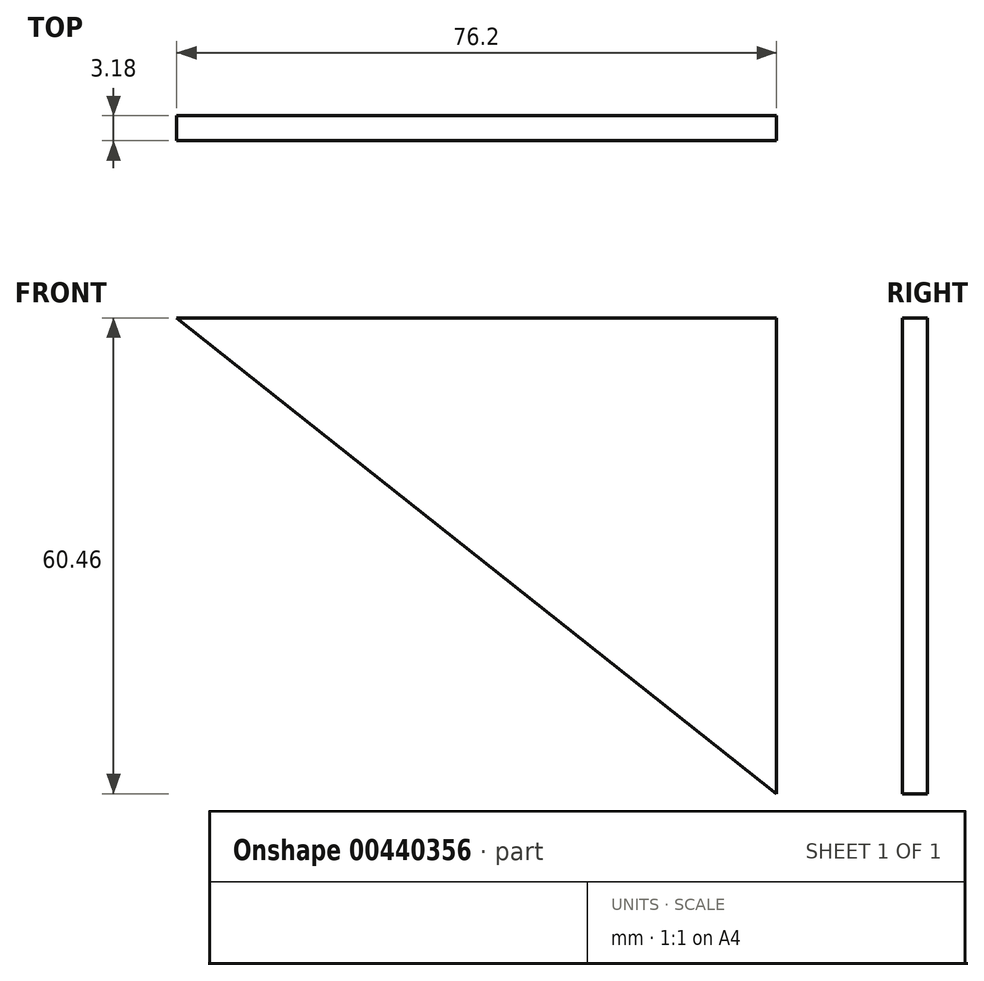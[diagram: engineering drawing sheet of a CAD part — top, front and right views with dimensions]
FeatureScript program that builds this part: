
annotation { "Feature Type Name" : "Feature", "Feature Type Description" : "" }
export const myFeature = defineFeature(function(context is Context, id is Id, definition is map)
    precondition{}
    {
        {
            var Q0;
            Q0=qCreatedBy(makeId("Front.planeOp"),FACE);
            var sketch = newSketch(context, id + "F0", { "sketchPlane" : qUnion([Q0])});
            skLineSegment(sketch, "E0.bottom", {"start": v(-38.1, 30.23) * mm, "end": v(38.1, 30.23) * mm});
            skLineSegment(sketch, "E0.right", {"start": v(38.1, 30.23) * mm, "end": v(38.1, -30.23) * mm});
            skPoint(sketch, "E0.middle", {"position": v(0, 0) * mm});
            skLineSegment(sketch, "E1", {"start": v(-38.1, 30.23) * mm, "end": v(38.1, -30.23) * mm});
            skSolve(sketch);
        }
        {
            var Q0;
            Q0=makeQuery(id+"F0.imprint","IMPRINT",FACE,{"disambiguationData":[TD([[makeQuery(id+"F0.imprint","IMPRINT",EDGE,{"derivedFrom":sQuery(id+"F0.wireOp",EDGE,"E0.bottom")}),-1.0]])]});
            extrude(context, id + "F1", {"entities" : qUnion([Q0]), "endBound" : BoundingType.SYMMETRIC, "depth" : 3.17 * mm});
        }
    });
